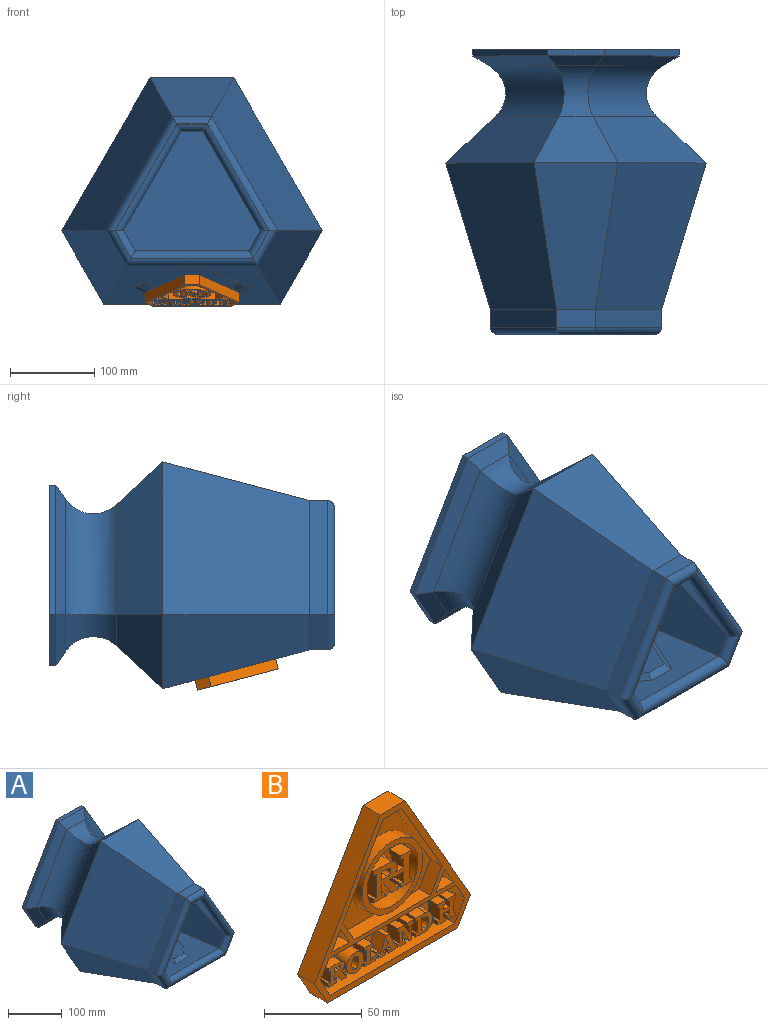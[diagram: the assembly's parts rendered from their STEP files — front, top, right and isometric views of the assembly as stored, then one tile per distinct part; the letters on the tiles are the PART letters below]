
ASSEMBLY  parts=2 mates=1
PART A: 95 faces, bbox 309.4x339x269.3 mm
  f0: cylinder r=52mm len=122.99mm, axis (0.5,0,0.87), area 510.7mm2, adj f1,f5,f7,f28
  f1: cylinder r=52mm len=28.89mm, axis (-0.5,0,0.87), area 111.9mm2, adj f0,f2,f12,f29
  f2: cylinder r=52mm len=139.5mm, axis (-1,0,0), area 506.3mm2, adj f1,f3,f11,f30
  f3: cylinder r=52mm len=28.89mm, axis (0.5,0,0.87), area 111.9mm2, adj f2,f4,f10,f31
  f4: cylinder r=52mm len=122.99mm, axis (-0.5,0,0.87), area 510.7mm2, adj f3,f5,f9,f32
  f5: cylinder r=52mm len=30.35mm, axis (1,0,0), area 106.1mm2, adj f0,f4,f8,f27
  f6: plane 182.95x159.72mm, normal (0,-1,0), area 99.4mm2, adj f83,f84,f85,f86,f87,f88,f89,f90
  f7: plane 168.42x124.19mm, normal (0.64,-0.68,-0.37), area 11527.2mm2, adj f0,f8,f12,f15
  f8: plane 84.15x50.6mm, normal (0,-0.68,-0.74), area 3939.1mm2, adj f5,f7,f9,f16
  f9: plane 168.42x124.19mm, normal (-0.64,-0.68,-0.37), area 11527.2mm2, adj f4,f8,f10,f17
  f10: plane 74.47x69.61mm, normal (-0.64,-0.68,0.36), area 4048.6mm2, adj f3,f9,f11,f18
  f11: plane 193.62x50.6mm, normal (0,-0.68,0.74), area 11460.5mm2, adj f2,f10,f12,f13
  f12: plane 74.47x69.61mm, normal (0.64,-0.68,0.36), area 4048.6mm2, adj f1,f7,f11,f14
  f13: plane 193.62x189.66mm, normal (0,0.26,0.97), area 19716.4mm2, adj f11,f14,f18,f20,f21,f22,f23,f24
  f14: plane 189.66x74.47mm, normal (0.84,0.26,0.48), area 11138mm2, adj f12,f13,f15,f91
  f15: plane 189.66x168.43mm, normal (0.84,0.26,-0.48), area 32462.9mm2, adj f7,f14,f16,f89
  f16: plane 189.66x84.15mm, normal (0,0.26,-0.97), area 10826.2mm2, adj f8,f15,f17,f90
  f17: plane 189.66x168.43mm, normal (-0.84,0.26,-0.48), area 32462.9mm2, adj f9,f16,f18,f92
  f18: plane 189.66x74.47mm, normal (-0.84,0.26,0.48), area 11138mm2, adj f10,f13,f17,f94
  f19: plane 129.29x109.1mm, normal (0,0.26,0.97), area 9660.8mm2, adj f20,f21,f22,f23,f24,f25
  f20: plane 34.06x8.56mm, normal (0,-0.5,0.86), area 297.2mm2, adj f13,f19,f21,f22
  f21: plane 94.93x59.73mm, normal (-0.61,-0.16,0.77), area 1061.6mm2, adj f13,f19,f20,f23
  f22: plane 94.93x59.73mm, normal (0.61,-0.16,0.77), area 1061.6mm2, adj f13,f19,f20,f24
  f23: plane 29.52x21.51mm, normal (-0.61,0.52,0.59), area 308.1mm2, adj f13,f19,f21,f25
  f24: plane 29.52x21.51mm, normal (0.61,0.52,0.59), area 308.1mm2, adj f13,f19,f22,f25
  f25: plane 110.54x8.56mm, normal (0,0.86,0.5), area 1054.1mm2, adj f13,f19,f23,f24
  f26: plane 165.66x144.73mm, normal (0,-1,0), area 15366mm2, adj f27,f28,f29,f30,f31,f32
  f27: plane 27.59x2.78mm, normal (0,0,1), area 76.8mm2, adj f5,f26,f28,f32
  f28: plane 119.41x69.04mm, normal (-0.87,0,0.5), area 383.7mm2, adj f0,f26,f27,f29
  f29: plane 25.31x14.47mm, normal (-0.87,0,-0.5), area 81.1mm2, adj f1,f26,f28,f30
  f30: plane 136.73x2.78mm, normal (0,0,-1), area 380.3mm2, adj f2,f26,f29,f31
  f31: plane 25.31x14.47mm, normal (0.87,0,-0.5), area 81.1mm2, adj f3,f26,f30,f32
  f32: plane 119.41x69.04mm, normal (0.87,0,0.5), area 383.7mm2, adj f4,f26,f27,f31
  f33: plane 46.4x21.42mm, normal (0,0,1), area 993.9mm2, adj f34,f38,f79,f86
  f34: plane 135.66x78.43mm, normal (-0.87,0,0.5), area 3356.8mm2, adj f33,f35,f80,f84
  f35: plane 41.66x23.8mm, normal (-0.87,0,-0.5), area 1027.8mm2, adj f34,f36,f81,f83
  f36: plane 155.65x21.42mm, normal (0,0,-1), area 3334.3mm2, adj f35,f37,f82,f85
  f37: plane 41.66x23.8mm, normal (0.87,0,-0.5), area 1027.8mm2, adj f36,f38,f77,f87
  f38: plane 135.66x78.43mm, normal (0.87,0,0.5), area 3356.8mm2, adj f33,f37,f78,f88
  f39: plane 244.78x213.32mm, normal (0,1,0), area 36536.2mm2, adj f40,f41,f42,f43,f44,f45
  f40: plane 176.54x8mm, normal (0,0,-1), area 1412.3mm2, adj f39,f41,f45,f46
  f41: plane 59.71x34.12mm, normal (-0.87,0,-0.5), area 550.2mm2, adj f39,f40,f42,f48
  f42: plane 153.61x88.8mm, normal (-0.87,0,0.5), area 1419.4mm2, adj f39,f41,f43,f49
  f43: plane 67.17x8mm, normal (0,0,1), area 537.3mm2, adj f39,f42,f44,f50
  f44: plane 153.61x88.8mm, normal (0.87,0,0.5), area 1419.4mm2, adj f39,f43,f45,f51
  f45: plane 59.71x34.12mm, normal (0.87,0,-0.5), area 550.2mm2, adj f39,f40,f44,f52
  f46: plane 176.54x16.68mm, normal (0,-0.82,-0.58), area 3404.1mm2, adj f40,f48,f52,f53
  f47: plane 117.82x99.49mm, normal (0,-0.26,-0.97), area 7813mm2, adj f54,f55,f56,f57,f58,f59
  f48: plane 59.71x43.8mm, normal (-0.5,-0.82,-0.29), area 1206.4mm2, adj f41,f46,f49,f60
  f49: plane 153.66x98.43mm, normal (-0.5,-0.82,0.29), area 3423.8mm2, adj f42,f48,f50,f61
  f50: plane 67.17x16.68mm, normal (0,-0.82,0.58), area 1173.9mm2, adj f43,f49,f51,f62
  f51: plane 153.66x98.43mm, normal (0.5,-0.82,0.29), area 3423.8mm2, adj f44,f50,f52,f63
  f52: plane 59.71x43.8mm, normal (0.5,-0.82,-0.29), area 1206.4mm2, adj f45,f46,f51,f64
  f53: cylinder r=40mm len=157.17mm, axis (-1,0,0), area 9742.8mm2, adj f46,f60,f64,f65
  f54: plane 87.28x54.16mm, normal (-0.61,0.16,-0.77), area 659.6mm2, adj f47,f55,f59,f66
  f55: plane 25.62x5.69mm, normal (0,0.5,-0.86), area 151mm2, adj f47,f54,f56,f67
  f56: plane 87.28x54.16mm, normal (0.61,0.16,-0.77), area 659.6mm2, adj f47,f55,f57,f68
  f57: plane 22.43x15.96mm, normal (0.61,-0.52,-0.59), area 158.3mm2, adj f47,f56,f58,f69
  f58: plane 102.05x5.69mm, normal (0,-0.86,-0.5), area 654.3mm2, adj f47,f57,f59,f70
  f59: plane 22.43x15.96mm, normal (-0.61,-0.52,-0.59), area 158.3mm2, adj f47,f54,f58,f71
  f60: cylinder r=40mm len=59.82mm, axis (-0.5,0,0.87), area 2416.5mm2, adj f48,f53,f61,f72
  f61: cylinder r=40mm len=145.47mm, axis (0.5,0,0.87), area 9821mm2, adj f49,f60,f62,f73
  f62: cylinder r=40mm len=59.82mm, axis (1,0,0), area 2309.7mm2, adj f50,f61,f63,f74
  f63: cylinder r=40mm len=145.47mm, axis (-0.5,0,0.87), area 9821mm2, adj f51,f62,f64,f75
  f64: cylinder r=40mm len=59.82mm, axis (0.5,0,0.87), area 2416.5mm2, adj f52,f53,f63,f76
  f65: plane 209.04x55.44mm, normal (0,0.68,-0.74), area 13523.9mm2, adj f53,f72,f76,f82
  f66: cylinder r=8mm len=94.86mm, axis (-0.5,-0.84,0.22), area 665.5mm2, adj f54,f67,f71,f82
  f67: cylinder r=8mm len=32.15mm, axis (1,0,0), area 180.4mm2, adj f55,f66,f68,f82
  f68: cylinder r=8mm len=94.86mm, axis (0.5,-0.84,0.22), area 665.5mm2, adj f56,f67,f69,f82
  f69: cylinder r=8mm len=30.02mm, axis (-0.5,-0.84,0.22), area 187.3mm2, adj f57,f68,f70,f82
  f70: cylinder r=8mm len=108.62mm, axis (-1,0,0), area 660.7mm2, adj f58,f69,f71,f82
  f71: cylinder r=8mm len=30.02mm, axis (0.5,-0.84,0.22), area 187.3mm2, adj f59,f66,f70,f82
  f72: plane 87.79x79.81mm, normal (-0.64,0.68,-0.36), area 5398.5mm2, adj f60,f65,f73,f81
  f73: plane 181.67x134.42mm, normal (-0.64,0.68,0.37), area 13589.5mm2, adj f61,f72,f74,f80
  f74: plane 99.48x55.44mm, normal (0,0.68,0.74), area 5277.5mm2, adj f62,f73,f75,f79
  f75: plane 181.67x134.42mm, normal (0.64,0.68,0.37), area 13589.5mm2, adj f63,f74,f76,f78
  f76: plane 87.79x79.81mm, normal (0.64,0.68,-0.36), area 5398.5mm2, adj f64,f65,f75,f77
  f77: plane 173.78x87.79mm, normal (0.84,-0.26,-0.48), area 13400.3mm2, adj f37,f76,f78,f82
  f78: plane 181.66x173.78mm, normal (0.84,-0.26,0.48), area 32930.4mm2, adj f38,f75,f77,f79
  f79: plane 173.78x99.48mm, normal (0,-0.26,0.97), area 13111.4mm2, adj f33,f74,f78,f80
  f80: plane 181.66x173.78mm, normal (-0.84,-0.26,0.48), area 32930.4mm2, adj f34,f73,f79,f81
  f81: plane 173.78x87.79mm, normal (-0.84,-0.26,-0.48), area 13400.3mm2, adj f35,f72,f80,f82
  f82: plane 209.04x173.78mm, normal (0,-0.26,-0.97), area 20940.1mm2, adj f36,f65,f66,f67,f68,f69,f70,f71
  f83: cylinder r=8.8mm len=46.02mm, axis (-0.5,0,0.87), area 612.1mm2, adj f6,f35,f84,f85
  f84: cylinder r=8.8mm len=140.06mm, axis (0.5,0,0.87), area 2115.1mm2, adj f6,f34,f83,f86
  f85: cylinder r=8.8mm len=155.65mm, axis (-1,0,0), area 2100.2mm2, adj f6,f36,f83,f87
  f86: cylinder r=8.8mm len=46.4mm, axis (1,0,0), area 590.3mm2, adj f6,f33,f84,f88
  f87: cylinder r=8.8mm len=46.02mm, axis (-0.5,0,-0.87), area 612.1mm2, adj f6,f37,f85,f88
  f88: cylinder r=8.8mm len=140.06mm, axis (0.5,0,-0.87), area 2115.1mm2, adj f6,f38,f86,f87
  f89: cylinder r=8.8mm len=131.11mm, axis (0.5,0,0.87), area 2244.3mm2, adj f6,f15,f90,f91
  f90: cylinder r=8.8mm len=36.03mm, axis (1,0,0), area 467.9mm2, adj f6,f16,f89,f92
  f91: cylinder r=8.8mm len=37.02mm, axis (-0.5,0,0.87), area 493.1mm2, adj f6,f14,f89,f93
  f92: cylinder r=8.8mm len=131.11mm, axis (0.5,0,-0.87), area 2244.3mm2, adj f6,f17,f90,f94
  f93: cylinder r=8.8mm len=145.22mm, axis (-1,0,0), area 2225.2mm2, adj f6,f13,f91,f94
  f94: cylinder r=8.8mm len=37.02mm, axis (-0.5,0,-0.87), area 493.1mm2, adj f6,f18,f92,f93
PART B: 202 faces, bbox 113.2x12.3x98.9 mm
  f0: plane 104.58x23.6mm, normal (0,-1,0), area 1616.9mm2, adj f21,f22,f23,f24,f25,f26,f76,f77
  f1: plane 37x37mm, normal (0,-1,0), area 707.7mm2, adj f32,f35,f36,f37,f38,f39,f40,f41
  f2: plane 113.21x98.92mm, normal (0,-1,0), area 1581.6mm2, adj f3,f4,f5,f6,f7,f8,f10,f11
  f3: plane 17.94x12.32mm, normal (0,0,1), area 221mm2, adj f2,f4,f8,f9
  f4: plane 82.4x47.64mm, normal (-0.87,0,0.5), area 1172.6mm2, adj f2,f3,f5,f9
  f5: plane 16.52x12.32mm, normal (-0.87,0,-0.5), area 234.4mm2, adj f2,f4,f6,f9
  f6: plane 94.33x12.32mm, normal (0,0,-1), area 1162.1mm2, adj f2,f5,f7,f9
  f7: plane 16.52x12.32mm, normal (0.87,0,-0.5), area 234.4mm2, adj f2,f6,f8,f9
  f8: plane 82.4x47.64mm, normal (0.87,0,0.5), area 1172.6mm2, adj f2,f3,f7,f9
  f9: plane 113.21x98.92mm, normal (0,1,0), area 7117.7mm2, adj f3,f4,f5,f6,f7,f8
  f10: plane 50.64x29.27mm, normal (-0.87,0,-0.5), area 491.3mm2, adj f2,f11,f15,f16
  f11: plane 13.39x8.4mm, normal (0,0,-1), area 112.4mm2, adj f2,f10,f12,f16
  f12: plane 50.64x29.27mm, normal (0.87,0,-0.5), area 491.3mm2, adj f2,f11,f13,f16
  f13: plane 14.54x8.4mm, normal (0.87,0,0.5), area 140.7mm2, adj f2,f12,f14,f16
  f14: plane 55.31x8.4mm, normal (0,0,1), area 464.6mm2, adj f2,f13,f15,f16
  f15: plane 14.54x8.4mm, normal (-0.87,0,0.5), area 140.7mm2, adj f2,f10,f14,f16
  f16: plane 71.93x65.18mm, normal (0,-1,0), area 1564.5mm2, adj f10,f11,f12,f13,f14,f15,f33
  f17: plane 11.22x8.4mm, normal (-0.87,0,-0.5), area 108.5mm2, adj f2,f18,f19,f20
  f18: plane 11.22x8.4mm, normal (0.87,0,-0.5), area 108.6mm2, adj f2,f17,f19,f20
  f19: plane 12.82x8.4mm, normal (0,0,1), area 107.7mm2, adj f2,f17,f18,f20
  f20: plane 12.82x11.22mm, normal (0,-1,0), area 71.9mm2, adj f17,f18,f19
  f21: plane 91.93x8.4mm, normal (0,0,-1), area 772.2mm2, adj f0,f2,f22,f26
  f22: plane 10.94x8.4mm, normal (0.87,0,-0.5), area 106.2mm2, adj f0,f2,f21,f23
  f23: plane 12.66x8.4mm, normal (0.87,0,0.5), area 122.4mm2, adj f0,f2,f22,f24
  f24: plane 90.11x8.4mm, normal (0,0,1), area 757mm2, adj f0,f2,f23,f25
  f25: plane 12.66x8.4mm, normal (-0.87,0,0.5), area 122.4mm2, adj f0,f2,f24,f26
  f26: plane 10.94x8.4mm, normal (-0.87,0,-0.5), area 106.2mm2, adj f0,f2,f21,f25
  f27: plane 11.22x8.4mm, normal (-0.87,0,-0.5), area 108.6mm2, adj f2,f28,f29,f30
  f28: plane 11.22x8.4mm, normal (0.87,0,-0.5), area 108.5mm2, adj f2,f27,f29,f30
  f29: plane 12.82x8.4mm, normal (0,0,1), area 107.7mm2, adj f2,f27,f28,f30
  f30: plane 12.82x11.22mm, normal (0,-1,0), area 71.9mm2, adj f27,f28,f29
  f31: plane 44x44mm, normal (0,-1,0), area 445.4mm2, adj f32,f33
  f32: cylinder r=18.5mm len=37mm, axis (0,1,0), area 976.5mm2, adj f1,f31
  f33: cylinder r=22mm len=44mm, axis (0,1,0), area 1161.2mm2, adj f16,f31
  f34: plane 27.82x19.77mm, normal (0,-1,0), area 335.8mm2, adj f35,f36,f37,f38,f39,f40,f41,f42
  f35: plane 8.4x6.57mm, normal (1,0,0), area 55.1mm2, adj f1,f34,f36,f66
  f36: plane 8.4x1.18mm, normal (0,0,-1), area 9.9mm2, adj f1,f34,f35,f37
  f37: plane 8.88x8.4mm, normal (-0.83,0,-0.56), area 90.4mm2, adj f1,f34,f36,f38
  f38: plane 8.4x4.96mm, normal (0,0,-1), area 41.7mm2, adj f1,f34,f37,f39
  f39: plane 8.4x2.32mm, normal (1,0,0), area 19.5mm2, adj f1,f34,f38,f40
  f40: plane 8.4x1.25mm, normal (0,0,1), area 10.5mm2, adj f1,f34,f39,f41
  f41: plane 8.4x6.57mm, normal (0.8,0,0.6), area 69mm2, adj f1,f34,f40,f42
  f42: plane 9.79x8.4mm, normal (0,0,-1), area 82.2mm2, adj f1,f34,f41,f43
  f43: plane 8.4x6.57mm, normal (-1,0,0), area 55.1mm2, adj f1,f34,f42,f44
  f44: plane 8.4x1.77mm, normal (0,0,1), area 14.9mm2, adj f1,f34,f43,f45
  f45: plane 8.4x2.32mm, normal (-1,0,0), area 19.5mm2, adj f1,f34,f44,f46
  f46: plane 8.4x7.84mm, normal (0,0,-1), area 65.9mm2, adj f1,f34,f45,f47
  f47: plane 8.4x2.32mm, normal (1,0,0), area 19.5mm2, adj f1,f34,f46,f48
  f48: plane 8.4x1.86mm, normal (0,0,1), area 15.6mm2, adj f1,f34,f47,f49
  f49: plane 14.8x8.4mm, normal (1,0,0), area 124.3mm2, adj f1,f34,f48,f50
  f50: plane 8.4x1.86mm, normal (0,0,-1), area 15.6mm2, adj f1,f34,f49,f51
  f51: plane 8.4x2.66mm, normal (1,0,0), area 22.3mm2, adj f1,f34,f50,f52
  f52: plane 8.4x7.91mm, normal (0,0,1), area 66.4mm2, adj f1,f34,f51,f53
  f53: plane 8.4x2.66mm, normal (-1,0,0), area 22.3mm2, adj f1,f34,f52,f54
  f54: plane 8.4x1.84mm, normal (0,0,-1), area 15.4mm2, adj f1,f34,f53,f55
  f55: plane 8.4x5.59mm, normal (-1,0,0), area 47mm2, adj f1,f34,f54,f56
  f56: plane 8.4x5.39mm, normal (0,0,1), area 45.3mm2, adj f1,f34,f55,f57
  f57: extruded ~8.4x8.25mm, area 87.2mm2, adj f1,f34,f56,f58
  f58: plane 12.82x8.4mm, normal (0,0,1), area 107.7mm2, adj f1,f34,f57,f59
  f59: plane 8.4x2.66mm, normal (-1,0,0), area 22.3mm2, adj f1,f34,f58,f60
  f60: plane 8.4x1.76mm, normal (0,0,-1), area 14.8mm2, adj f1,f34,f59,f61
  f61: plane 14.8x8.4mm, normal (-1,0,0), area 124.3mm2, adj f1,f34,f60,f62
  f62: plane 8.4x2.03mm, normal (0,0,1), area 17.1mm2, adj f1,f34,f61,f63
  f63: plane 8.4x2.32mm, normal (-1,0,0), area 19.5mm2, adj f1,f34,f62,f65
  f64: plane 8.4x4.64mm, normal (0,0,-1), area 38.9mm2, adj f34,f68,f69,f71
  f65: plane 8.4x7.91mm, normal (0,0,-1), area 66.4mm2, adj f1,f34,f63,f67
  f66: plane 8.4x1.98mm, normal (0,0,1), area 16.6mm2, adj f1,f34,f35,f67
  f67: plane 8.4x2.32mm, normal (1,0,0), area 19.5mm2, adj f1,f34,f65,f66
  f68: extruded ~8.4x5.05mm, area 61.6mm2, adj f34,f64,f70,f71
  f69: plane 8.4x5.05mm, normal (1,0,0), area 42.4mm2, adj f34,f64,f70,f71
  f70: plane 8.4x4.64mm, normal (0,0,1), area 38.9mm2, adj f34,f68,f69,f71
  f71: plane 6.84x5.05mm, normal (0,-1,0), area 31.9mm2, adj f64,f68,f69,f70
  f72: plane 13.19x11.85mm, normal (0,-1,0), area 99.3mm2, adj f73,f74,f75,f76,f77,f78,f79,f80
  f73: plane 8.4x3.47mm, normal (0,0,1), area 29.2mm2, adj f72,f74,f93,f94
  f74: plane 8.4x2.67mm, normal (1,0,0), area 22.4mm2, adj f72,f73,f75,f94
  f75: plane 8.4x3.47mm, normal (0,0,-1), area 29.2mm2, adj f72,f74,f93,f94
  f76: plane 9.22x8.4mm, normal (0,0,1), area 77.5mm2, adj f0,f72,f77,f92
  f77: plane 8.4x2.24mm, normal (-1,0,0), area 18.8mm2, adj f0,f72,f76,f78
  f78: plane 8.4x1.31mm, normal (0,0,-1), area 11mm2, adj f0,f72,f77,f79
  f79: plane 8.4x7.28mm, normal (-1,0,0), area 61.1mm2, adj f0,f72,f78,f80
  f80: plane 8.4x1.44mm, normal (0,0,1), area 12.1mm2, adj f0,f72,f79,f81
  f81: plane 8.4x2.29mm, normal (-1,0,0), area 19.2mm2, adj f0,f72,f80,f82
  f82: plane 8.4x6.22mm, normal (0,0,-1), area 52.2mm2, adj f0,f72,f81,f83
  f83: plane 8.4x2.24mm, normal (1,0,0), area 18.8mm2, adj f0,f72,f82,f84
  f84: plane 8.4x1.82mm, normal (0,0,1), area 15.3mm2, adj f0,f72,f83,f85
  f85: plane 8.4x3mm, normal (1,0,0), area 25.2mm2, adj f0,f72,f84,f86
  f86: plane 8.4x1.06mm, normal (0,0,-1), area 8.9mm2, adj f0,f72,f85,f87
  f87: plane 8.4x5.29mm, normal (-0.8,0,-0.6), area 55.7mm2, adj f0,f72,f86,f88
  f88: plane 8.4x3.74mm, normal (0,0,-1), area 31.4mm2, adj f0,f72,f87,f89
  f89: plane 8.4x1.44mm, normal (1,0,0), area 12.1mm2, adj f0,f72,f88,f90
  f90: plane 8.4x0.87mm, normal (0,0,1), area 7.3mm2, adj f0,f72,f89,f91
  f91: plane 8.4x3.89mm, normal (0.8,0,0.61), area 41.1mm2, adj f0,f72,f90,f92
  f92: extruded ~8.4x6.52mm, area 73.1mm2, adj f0,f72,f76,f91
  f93: extruded ~8.4x2.67mm, area 30.7mm2, adj f72,f73,f75,f94
  f94: plane 4.78x2.67mm, normal (0,-1,0), area 11.3mm2, adj f73,f74,f75,f93
  f95: plane 12.62x12.62mm, normal (0,-1,0), area 93mm2, adj f96,f97,f98
  f96: extruded ~8.4x7.91mm, area 87.5mm2, adj f95,f97,f99
  f97: extruded ~8.4x7.91mm, area 87.5mm2, adj f95,f96,f99
  f98: cylinder r=6.31mm len=12.62mm, axis (0,1,0), area 333.1mm2, adj f0,f95
  f99: plane 7.91x6.67mm, normal (0,-1,0), area 32.2mm2, adj f96,f97
  f100: plane 11.85x10.62mm, normal (0,-1,0), area 58.2mm2, adj f101,f102,f103,f104,f105,f106,f107,f108
  f101: plane 8.4x1.57mm, normal (0,0,1), area 13.2mm2, adj f0,f100,f102,f115
  f102: plane 8.4x1.99mm, normal (-1,0,0), area 16.8mm2, adj f0,f100,f101,f103
  f103: plane 8.4x7.87mm, normal (0,0,-1), area 66.1mm2, adj f0,f100,f102,f104
  f104: plane 8.4x3.69mm, normal (0.8,0,-0.6), area 38.6mm2, adj f0,f100,f103,f105
  f105: plane 8.4x0.93mm, normal (1,0,0), area 7.8mm2, adj f0,f100,f104,f106
  f106: plane 8.4x1.99mm, normal (0,0,1), area 16.7mm2, adj f0,f100,f105,f107
  f107: plane 8.4x0.93mm, normal (-1,0,0), area 7.8mm2, adj f0,f100,f106,f108
  f108: plane 8.4x1.91mm, normal (-0.66,0,0.75), area 21.4mm2, adj f0,f100,f107,f109
  f109: plane 8.4x2.29mm, normal (0,0,1), area 19.2mm2, adj f0,f100,f108,f110
  f110: plane 8.4x7.57mm, normal (1,0,0), area 63.6mm2, adj f0,f100,f109,f111
  f111: plane 8.4x1.48mm, normal (0,0,-1), area 12.5mm2, adj f0,f100,f110,f112
  f112: plane 8.4x2.28mm, normal (1,0,0), area 19.2mm2, adj f0,f100,f111,f113
  f113: plane 8.4x5.92mm, normal (0,0,1), area 49.8mm2, adj f0,f100,f112,f114
  f114: plane 8.4x2.28mm, normal (-1,0,0), area 19.2mm2, adj f0,f100,f113,f116
  f115: plane 8.4x7.57mm, normal (-1,0,0), area 63.6mm2, adj f0,f100,f101,f116
  f116: plane 8.4x1.57mm, normal (0,0,-1), area 13.2mm2, adj f0,f100,f114,f115
  f117: plane 13.17x11.85mm, normal (0,-1,0), area 75.1mm2, adj f118,f119,f120,f121,f122,f123,f124,f125
  f118: plane 8.4x2.81mm, normal (-0.92,0,-0.38), area 25.6mm2, adj f117,f119,f136,f137
  f119: plane 8.4x2.36mm, normal (0,0,1), area 19.8mm2, adj f117,f118,f136,f137
  f120: plane 8.4x2.45mm, normal (0,0,1), area 20.6mm2, adj f0,f117,f121,f135
  f121: plane 9.86x8.4mm, normal (-0.92,0,0.39), area 89.8mm2, adj f0,f117,f120,f122
  f122: plane 8.4x1.01mm, normal (0,0,1), area 8.4mm2, adj f0,f117,f121,f123
  f123: plane 8.4x1.99mm, normal (-1,0,0), area 16.8mm2, adj f0,f117,f122,f124
  f124: plane 8.4x4.72mm, normal (0,0,-1), area 39.7mm2, adj f0,f117,f123,f125
  f125: plane 8.4x1.99mm, normal (1,0,0), area 16.8mm2, adj f0,f117,f124,f126
  f126: plane 8.4x1.64mm, normal (0,0,1), area 13.8mm2, adj f0,f117,f125,f127
  f127: plane 8.4x1.9mm, normal (0.92,0,-0.39), area 17.3mm2, adj f0,f117,f126,f128
  f128: plane 8.4x3.85mm, normal (0,0,-1), area 32.4mm2, adj f0,f117,f127,f129
  f129: plane 8.4x1.9mm, normal (-0.92,0,-0.38), area 17.3mm2, adj f0,f117,f128,f130
  f130: plane 8.4x1.86mm, normal (0,0,1), area 15.6mm2, adj f0,f117,f129,f131
  f131: plane 8.4x1.99mm, normal (-1,0,0), area 16.8mm2, adj f0,f117,f130,f132
  f132: plane 8.4x6.5mm, normal (0,0,-1), area 54.6mm2, adj f0,f117,f131,f133
  f133: plane 8.4x1.99mm, normal (1,0,0), area 16.8mm2, adj f0,f117,f132,f134
  f134: plane 8.4x1.45mm, normal (0,0,1), area 12.2mm2, adj f0,f117,f133,f135
  f135: plane 9.86x8.4mm, normal (0.92,0,0.38), area 89.7mm2, adj f0,f117,f120,f134
  f136: plane 8.4x2.81mm, normal (0.92,0,-0.39), area 25.6mm2, adj f117,f118,f119,f137
  f137: plane 2.81x2.36mm, normal (0,-1,0), area 3.3mm2, adj f118,f119,f136
  f138: plane 11.85x11.47mm, normal (0,-1,0), area 89mm2, adj f139,f140,f141,f142,f143,f144,f145,f146
  f139: plane 8.4x2.28mm, normal (-1,0,0), area 19.2mm2, adj f0,f138,f140,f157
  f140: plane 8.4x1.28mm, normal (0,0,-1), area 10.7mm2, adj f0,f138,f139,f141
  f141: plane 8.4x7.57mm, normal (-1,0,0), area 63.6mm2, adj f0,f138,f140,f142
  f142: plane 8.4x1.17mm, normal (0,0,1), area 9.8mm2, adj f0,f138,f141,f143
  f143: plane 8.4x1.99mm, normal (-1,0,0), area 16.8mm2, adj f0,f138,f142,f144
  f144: plane 8.4x5.41mm, normal (0,0,-1), area 45.4mm2, adj f0,f138,f143,f145
  f145: plane 8.4x1.99mm, normal (1,0,0), area 16.8mm2, adj f0,f138,f144,f146
  f146: plane 8.4x1.93mm, normal (0,0,1), area 16.2mm2, adj f0,f138,f145,f147
  f147: plane 8.4x6.54mm, normal (1,0,0), area 54.9mm2, adj f0,f138,f146,f148
  f148: plane 8.53x8.4mm, normal (-0.88,0,-0.48), area 81.8mm2, adj f0,f138,f147,f149
  f149: plane 8.4x1.91mm, normal (0,0,-1), area 16mm2, adj f0,f138,f148,f150
  f150: plane 9.57x8.4mm, normal (1,0,0), area 80.4mm2, adj f0,f138,f149,f151
  f151: plane 8.4x1.29mm, normal (0,0,-1), area 10.8mm2, adj f0,f138,f150,f152
  f152: plane 8.4x2.28mm, normal (1,0,0), area 19.2mm2, adj f0,f138,f151,f153
  f153: plane 8.4x4.53mm, normal (0,0,1), area 38mm2, adj f0,f138,f152,f154
  f154: plane 8.4x2.28mm, normal (-1,0,0), area 19.2mm2, adj f0,f138,f153,f155
  f155: plane 8.4x1.33mm, normal (0,0,-1), area 11.1mm2, adj f0,f138,f154,f156
  f156: plane 8.4x4.21mm, normal (-1,0,0), area 35.4mm2, adj f0,f138,f155,f158
  f157: plane 8.4x4.71mm, normal (0,0,1), area 39.5mm2, adj f0,f138,f139,f158
  f158: plane 8.4x6.5mm, normal (0.88,0,0.48), area 62.2mm2, adj f0,f138,f156,f157
  f159: plane 13.41x11.85mm, normal (0,-1,0), area 87.6mm2, adj f160,f161,f162,f163,f164,f165,f166,f167
  f160: plane 8.4x2.28mm, normal (-1,0,0), area 19.2mm2, adj f0,f159,f161,f167
  f161: plane 8.4x1.11mm, normal (0,0,-1), area 9.3mm2, adj f0,f159,f160,f162
  f162: plane 8.4x7.57mm, normal (-1,0,0), area 63.6mm2, adj f0,f159,f161,f163
  f163: plane 8.4x1.11mm, normal (0,0,1), area 9.3mm2, adj f0,f159,f162,f164
  f164: plane 8.4x1.99mm, normal (-1,0,0), area 16.8mm2, adj f0,f159,f163,f166
  f165: plane 8.4x2.88mm, normal (0,0,-1), area 24.2mm2, adj f159,f169,f170,f172
  f166: plane 8.4x6.99mm, normal (0,0,-1), area 58.7mm2, adj f0,f159,f164,f168
  f167: plane 8.4x6.99mm, normal (0,0,1), area 58.7mm2, adj f0,f159,f160,f168
  f168: extruded ~11.85x8.4mm, area 146.4mm2, adj f0,f159,f166,f167
  f169: extruded ~8.4x7.57mm, area 79.9mm2, adj f159,f165,f171,f172
  f170: plane 8.4x7.57mm, normal (1,0,0), area 63.6mm2, adj f159,f165,f171,f172
  f171: plane 8.4x2.88mm, normal (0,0,1), area 24.2mm2, adj f159,f169,f170,f172
  f172: plane 7.57x5.73mm, normal (0,-1,0), area 34.9mm2, adj f165,f169,f170,f171
  f173: plane 12.7x12.68mm, normal (0,-1,0), area 106.3mm2, adj f174,f175,f176,f177,f178,f179,f180,f181
  f174: plane 8.4x2.08mm, normal (-1,0,0), area 17.5mm2, adj f0,f173,f175,f200
  f175: plane 8.4x1.42mm, normal (0,0,-1), area 11.9mm2, adj f0,f173,f174,f176
  f176: plane 8.4x8.24mm, normal (-1,0,0), area 69.2mm2, adj f0,f173,f175,f177
  f177: plane 8.4x1.35mm, normal (0,0,1), area 11.3mm2, adj f0,f173,f176,f178
  f178: plane 8.4x2.35mm, normal (-1,0,0), area 19.7mm2, adj f0,f173,f177,f179
  f179: plane 8.4x5.7mm, normal (0,0,-1), area 47.9mm2, adj f0,f173,f178,f180
  f180: plane 8.4x2.35mm, normal (1,0,0), area 19.7mm2, adj f0,f173,f179,f181
  f181: plane 8.4x1.48mm, normal (0,0,1), area 12.4mm2, adj f0,f173,f180,f182
  f182: plane 8.4x2.96mm, normal (1,0,0), area 24.9mm2, adj f0,f173,f181,f183
  f183: plane 8.4x4.26mm, normal (0,0,-1), area 35.8mm2, adj f0,f173,f182,f184
  f184: plane 8.4x2.96mm, normal (-1,0,0), area 24.9mm2, adj f0,f173,f183,f185
  f185: plane 8.4x1.62mm, normal (0,0,1), area 13.6mm2, adj f0,f173,f184,f186
  f186: plane 8.4x2.35mm, normal (-1,0,0), area 19.7mm2, adj f0,f173,f185,f187
  f187: plane 8.4x5.77mm, normal (0,0,-1), area 48.5mm2, adj f0,f173,f186,f188
  f188: plane 8.4x2.35mm, normal (1,0,0), area 19.7mm2, adj f0,f173,f187,f189
  f189: plane 8.4x1.43mm, normal (0,0,1), area 12mm2, adj f0,f173,f188,f190
  f190: plane 8.4x8.24mm, normal (1,0,0), area 69.2mm2, adj f0,f173,f189,f191
  f191: plane 8.4x1.36mm, normal (0,0,-1), area 11.4mm2, adj f0,f173,f190,f192
  f192: plane 8.4x2.08mm, normal (1,0,0), area 17.5mm2, adj f0,f173,f191,f193
  f193: plane 8.4x5.64mm, normal (0,0,1), area 47.4mm2, adj f0,f173,f192,f194
  f194: plane 8.4x2.08mm, normal (-1,0,0), area 17.5mm2, adj f0,f173,f193,f195
  f195: plane 8.4x1.58mm, normal (0,0,-1), area 13.3mm2, adj f0,f173,f194,f196
  f196: plane 8.4x3.08mm, normal (-1,0,0), area 25.8mm2, adj f0,f173,f195,f197
  f197: plane 8.4x4.27mm, normal (0,0,1), area 35.8mm2, adj f0,f173,f196,f198
  f198: plane 8.4x3.08mm, normal (1,0,0), area 25.8mm2, adj f0,f173,f197,f199
  f199: plane 8.4x1.52mm, normal (0,0,-1), area 12.8mm2, adj f0,f173,f198,f201
  f200: plane 8.4x5.82mm, normal (0,0,1), area 48.9mm2, adj f0,f173,f174,f201
  f201: plane 8.4x2.08mm, normal (1,0,0), area 17.5mm2, adj f0,f173,f199,f200
PLACE A t=(-53.75,-40.31,149.67)mm
PLACE B rot(axis=(1,0,0),75.2deg) t=(-309.59,-202.26,26.5)mm
MATE fastened B.f9 <-> A.f82  axis (0,0.26,0.97) through (-305.75,-204.39,27.06)mm
